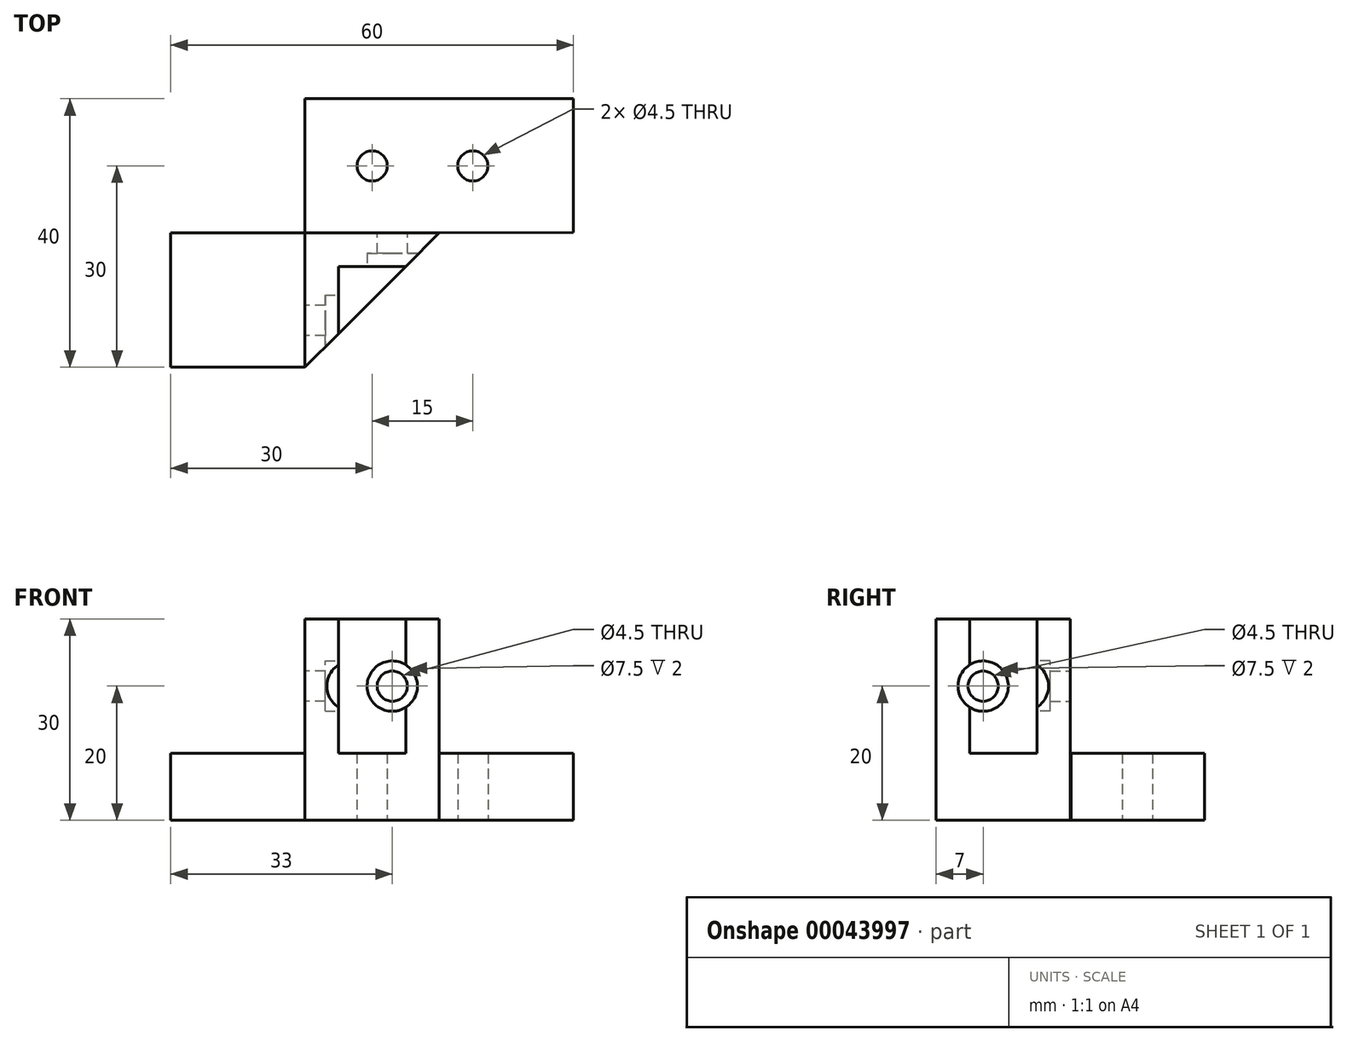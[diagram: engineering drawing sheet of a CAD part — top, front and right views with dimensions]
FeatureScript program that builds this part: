
annotation { "Feature Type Name" : "Feature", "Feature Type Description" : "" }
export const myFeature = defineFeature(function(context is Context, id is Id, definition is map)
    precondition{}
    {
        {
            var Q0;
            Q0=qCreatedBy(makeId("Top.planeOp"),FACE);
            var sketch = newSketch(context, id + "F0", { "sketchPlane" : qUnion([Q0])});
            skLineSegment(sketch, "E0.top", {"start": v(0, 20) * mm, "end": v(20, 20) * mm});
            skLineSegment(sketch, "E0.left", {"start": v(0, 0) * mm, "end": v(0, 20) * mm});
            skLineSegment(sketch, "E1", {"start": v(60, 40) * mm, "end": v(20, 40) * mm});
            skLineSegment(sketch, "E2", {"start": v(20, 40) * mm, "end": v(20, 20) * mm});
            skLineSegment(sketch, "E3", {"start": v(60, 40) * mm, "end": v(60, 20.1) * mm});
            skLineSegment(sketch, "E4", {"start": v(60, 20.1) * mm, "end": v(40, 20) * mm});
            skPoint(sketch, "E5.orphan", {"position": v(49.94, 0) * mm});
            skLineSegment(sketch, "E6", {"start": v(20, 30) * mm, "end": v(30, 30) * mm, "construction": true});
            skCircle(sketch, "E7", {"center": v(30, 30) * mm, "radius": 2.25 * mm});
            skLineSegment(sketch, "E8", {"start": v(30, 30) * mm, "end": v(45, 30) * mm, "construction": true});
            skCircle(sketch, "E9", {"center": v(45, 30) * mm, "radius": 2.25 * mm});
            skLineSegment(sketch, "E10", {"start": v(0, 0) * mm, "end": v(20, 0) * mm});
            skLineSegment(sketch, "E11", {"start": v(20, 0) * mm, "end": v(40, 20) * mm});
            skSolve(sketch);
        }
        {
            var Q0;
            Q0 = qSketchRegion(id + "F0", true);
            extrude(context, id + "F1", {"entities" : qUnion([Q0]), "depth" : 10 * mm});
        }
        {
            var Q0;
            Q0=makeQuery(id+"F1.opExtrude","CAP_FACE",FACE,{"disambiguationData":[OSD([sQuery(id+"F0.wireOp",EDGE,"E0.top"),sQuery(id+"F0.wireOp",EDGE,"E0.left"),sQuery(id+"F0.wireOp",EDGE,"E1"),sQuery(id+"F0.wireOp",EDGE,"E2"),sQuery(id+"F0.wireOp",EDGE,"E3"),sQuery(id+"F0.wireOp",EDGE,"E4"),sQuery(id+"F0.wireOp",EDGE,"E7"),sQuery(id+"F0.wireOp",EDGE,"E9"),sQuery(id+"F0.wireOp",EDGE,"E10"),sQuery(id+"F0.wireOp",EDGE,"E11")])],"isStart":false});
            var sketch = newSketch(context, id + "F2", { "sketchPlane" : qUnion([Q0])});
            skLineSegment(sketch, "E12", {"start": v(20, 20) * mm, "end": v(40, 20) * mm});
            skLineSegment(sketch, "E13", {"start": v(20, 20) * mm, "end": v(20, 0) * mm});
            skLineSegment(sketch, "E14", {"start": v(20, 10) * mm, "end": v(25, 10) * mm, "construction": true});
            skLineSegment(sketch, "E15", {"start": v(30, 20) * mm, "end": v(30, 15) * mm, "construction": true});
            skLineSegment(sketch, "E16", {"start": v(30, 15) * mm, "end": v(25, 15) * mm});
            skLineSegment(sketch, "E17", {"start": v(25, 15) * mm, "end": v(25, 10) * mm});
            skLineSegment(sketch, "E18", {"start": v(25, 10) * mm, "end": v(25, 5) * mm});
            skLineSegment(sketch, "E19", {"start": v(25, 5) * mm, "end": v(20, 0) * mm});
            skLineSegment(sketch, "E20", {"start": v(30, 15) * mm, "end": v(35, 15) * mm});
            skLineSegment(sketch, "E21", {"start": v(35, 15) * mm, "end": v(40, 20) * mm});
            skSolve(sketch);
        }
        {
            var Q0;
            Q0 = qSketchRegion(id + "F2", true);
            extrude(context, id + "F3", {"entities" : qUnion([Q0]), "operationType" : NewBodyOperationType.ADD, "depth" : 20 * mm});
        }
        {
            var Q0;
            Q0=makeQuery(id+"F3.opExtrude","SWEPT_FACE",FACE,{"disambiguationData":[OSD([sQuery(id+"F2.wireOp",EDGE,"E13")])]});
            var sketch = newSketch(context, id + "F4", { "sketchPlane" : qUnion([Q0])});
            skCircle(sketch, "E22", {"center": v(-7, 20) * mm, "radius": 2.25 * mm});
            skSolve(sketch);
        }
        {
            var Q0;
            Q0=makeQuery(id+"F4.imprint","IMPRINT",FACE,{"disambiguationData":[TD([[makeQuery(id+"F4.imprint","IMPRINT",EDGE,{"derivedFrom":sQuery(id+"F4.wireOp",EDGE,"E22")}),1.0]])]});
            var Q1;
            Q1=sQuery(id+"F4.wireOp",EDGE,"c6b93264-ce8d-4e4d-8a6d-3ec076cf6517");
            extrude(context, id + "F5", {"entities" : qUnion([Q0]), "operationType" : NewBodyOperationType.REMOVE, "surfaceEntities" : qUnion([Q1]), "oppositeDirection" : true, "depth" : 5 * mm});
        }
        {
            var Q0;
            Q0=makeQuery(id+"F3.opExtrude","SWEPT_FACE",FACE,{"disambiguationData":[OSD([sQuery(id+"F2.wireOp",EDGE,"E12")])]});
            var sketch = newSketch(context, id + "F6", { "sketchPlane" : qUnion([Q0])});
            skCircle(sketch, "E23", {"center": v(-33, 20) * mm, "radius": 2.25 * mm});
            skSolve(sketch);
        }
        {
            var Q0;
            Q0=makeQuery(id+"F6.imprint","IMPRINT",FACE,{"disambiguationData":[TD([[makeQuery(id+"F6.imprint","IMPRINT",EDGE,{"derivedFrom":sQuery(id+"F6.wireOp",EDGE,"E23")}),1.0]])]});
            extrude(context, id + "F7", {"entities" : qUnion([Q0]), "operationType" : NewBodyOperationType.REMOVE, "oppositeDirection" : true, "depth" : 5 * mm});
        }
        {
            var Q0;
            Q0=makeQuery(id+"F3.opExtrude","SWEPT_FACE",FACE,{"disambiguationData":[OSD([sQuery(id+"F2.wireOp",EDGE,"E16"),sQuery(id+"F2.wireOp",EDGE,"E20")])]});
            var sketch = newSketch(context, id + "F8", { "sketchPlane" : qUnion([Q0])});
            skLineSegment(sketch, "E24", {"start": v(30, 30) * mm, "end": v(30, 10) * mm, "construction": true});
            skCircle(sketch, "E25", {"center": v(33, 20) * mm, "radius": 3.75 * mm});
            skSolve(sketch);
        }
        {
            var Q0;
            Q0 = qSketchRegion(id + "F8", true);
            extrude(context, id + "F9", {"entities" : qUnion([Q0]), "operationType" : NewBodyOperationType.REMOVE, "oppositeDirection" : true, "depth" : 2 * mm});
        }
        {
            var Q0;
            Q0=makeQuery(id+"F3.opExtrude","SWEPT_FACE",FACE,{"disambiguationData":[OSD([sQuery(id+"F2.wireOp",EDGE,"E17"),sQuery(id+"F2.wireOp",EDGE,"E18")])]});
            var sketch = newSketch(context, id + "F10", { "sketchPlane" : qUnion([Q0])});
            skCircle(sketch, "E26", {"center": v(7, 20) * mm, "radius": 3.75 * mm});
            skSolve(sketch);
        }
        {
            var Q0;
            Q0 = qSketchRegion(id + "F10", true);
            extrude(context, id + "F11", {"entities" : qUnion([Q0]), "operationType" : NewBodyOperationType.REMOVE, "oppositeDirection" : true, "depth" : 2 * mm});
        }
    });
